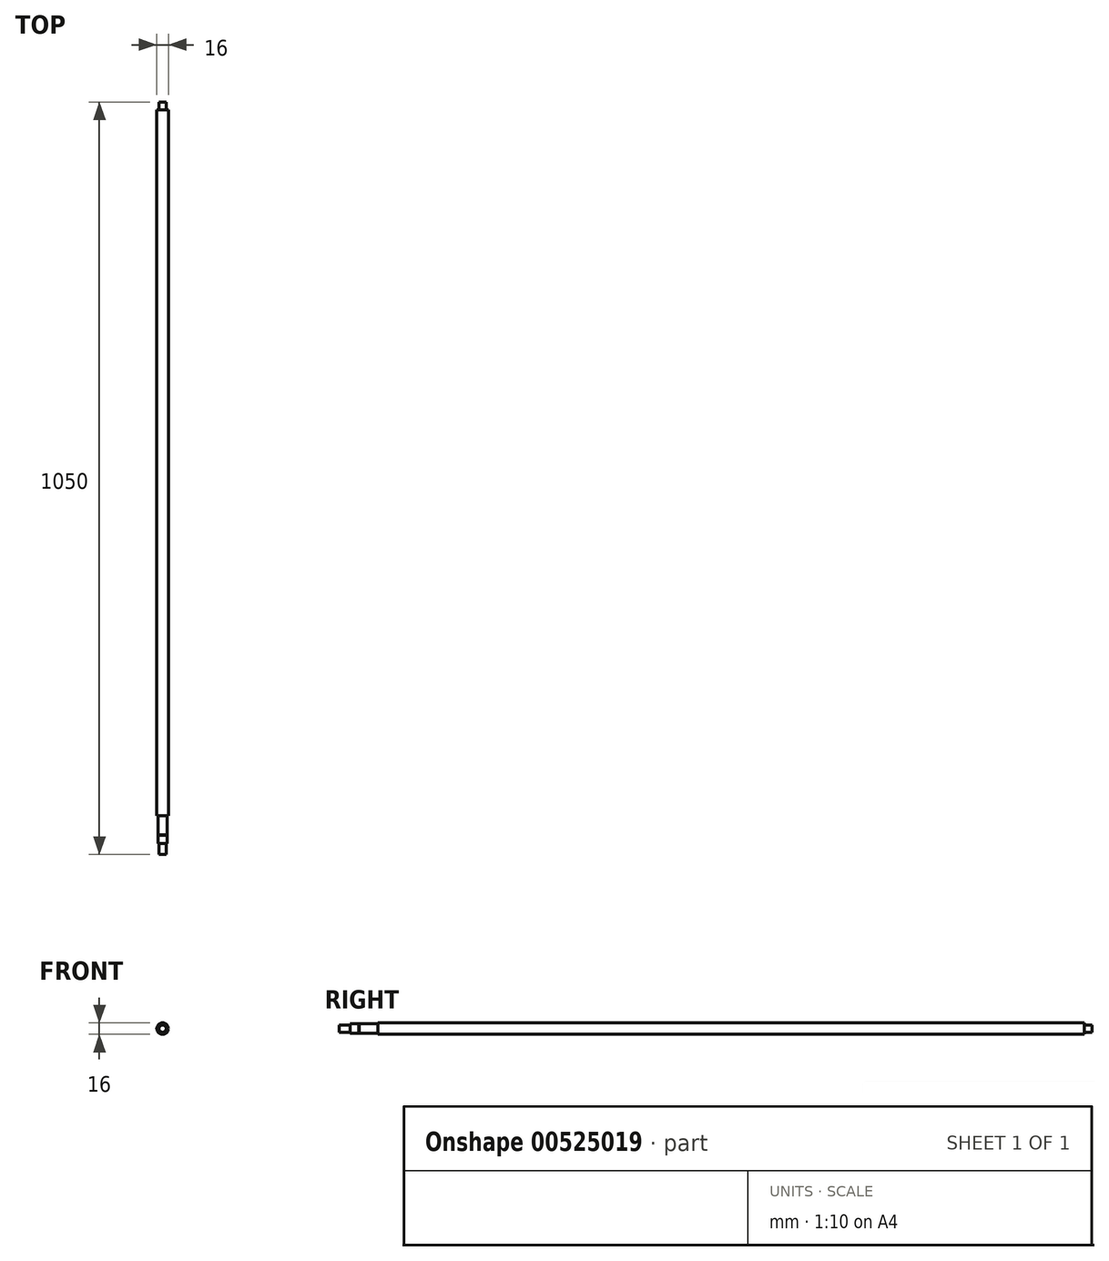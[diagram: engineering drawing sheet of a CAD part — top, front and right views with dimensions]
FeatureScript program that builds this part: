
annotation { "Feature Type Name" : "Feature", "Feature Type Description" : "" }
export const myFeature = defineFeature(function(context is Context, id is Id, definition is map)
    precondition{}
    {
        {
            var Q0;
            Q0=qCreatedBy(makeId("Right.planeOp"),FACE);
            var sketch = newSketch(context, id + "F0", { "sketchPlane" : qUnion([Q0])});
            skLineSegment(sketch, "E0.bottom", {"start": v(-492.5, 0) * mm, "end": v(492.5, 0) * mm});
            skLineSegment(sketch, "E0.top", {"start": v(-492.5, 8) * mm, "end": v(492.5, 8) * mm});
            skLineSegment(sketch, "E0.left", {"start": v(-492.5, 0) * mm, "end": v(-492.5, 8) * mm});
            skLineSegment(sketch, "E0.right", {"start": v(492.5, 0) * mm, "end": v(492.5, 8) * mm});
            skLineSegment(sketch, "E1.bottom", {"start": v(492.5, 5) * mm, "end": v(503.5, 5) * mm});
            skLineSegment(sketch, "E1.top", {"start": v(492.5, 0) * mm, "end": v(503.5, 0) * mm});
            skLineSegment(sketch, "E1.left", {"start": v(492.5, 5) * mm, "end": v(492.5, 0) * mm});
            skLineSegment(sketch, "E1.right", {"start": v(503.5, 5) * mm, "end": v(503.5, 0) * mm});
            skLineSegment(sketch, "E2.bottom", {"start": v(-492.5, 6.54) * mm, "end": v(-519, 6.54) * mm});
            skLineSegment(sketch, "E2.top", {"start": v(-492.5, 0) * mm, "end": v(-531.5, 0) * mm});
            skLineSegment(sketch, "E2.left", {"start": v(-492.5, 6.54) * mm, "end": v(-492.5, 0) * mm});
            skLineSegment(sketch, "E2.right", {"start": v(-531.5, 6.54) * mm, "end": v(-531.5, 5) * mm});
            skLineSegment(sketch, "E3.bottom", {"start": v(-531.5, 5) * mm, "end": v(-546.5, 5) * mm});
            skLineSegment(sketch, "E3.top", {"start": v(-432.3, 0) * mm, "end": v(-546.5, 0) * mm});
            skLineSegment(sketch, "E3.right", {"start": v(-546.5, 5) * mm, "end": v(-546.5, 0) * mm});
            skLineSegment(sketch, "E4", {"start": v(-519.5, 6.54) * mm, "end": v(-519.5, 6.04) * mm});
            skLineSegment(sketch, "E5", {"start": v(-519.5, 6.04) * mm, "end": v(-519, 6.04) * mm});
            skLineSegment(sketch, "E6", {"start": v(-519, 6.04) * mm, "end": v(-519, 6.54) * mm});
            skLineSegment(sketch, "E7.trimOffspring", {"start": v(-519.5, 6.54) * mm, "end": v(-531.5, 6.54) * mm});
            skSolve(sketch);
        }
        {
            var Q0;
            Q0 = qSketchRegion(id + "F0", true);
            var Q1;
            Q1=sQuery(id+"F0.wireOp",EDGE,"E0.bottom");
            revolve(context, id + "F1", {"entities" : qUnion([Q0]), "axis" : qUnion([Q1]), "revolveType" : RevolveType.FULL});
        }
    });
